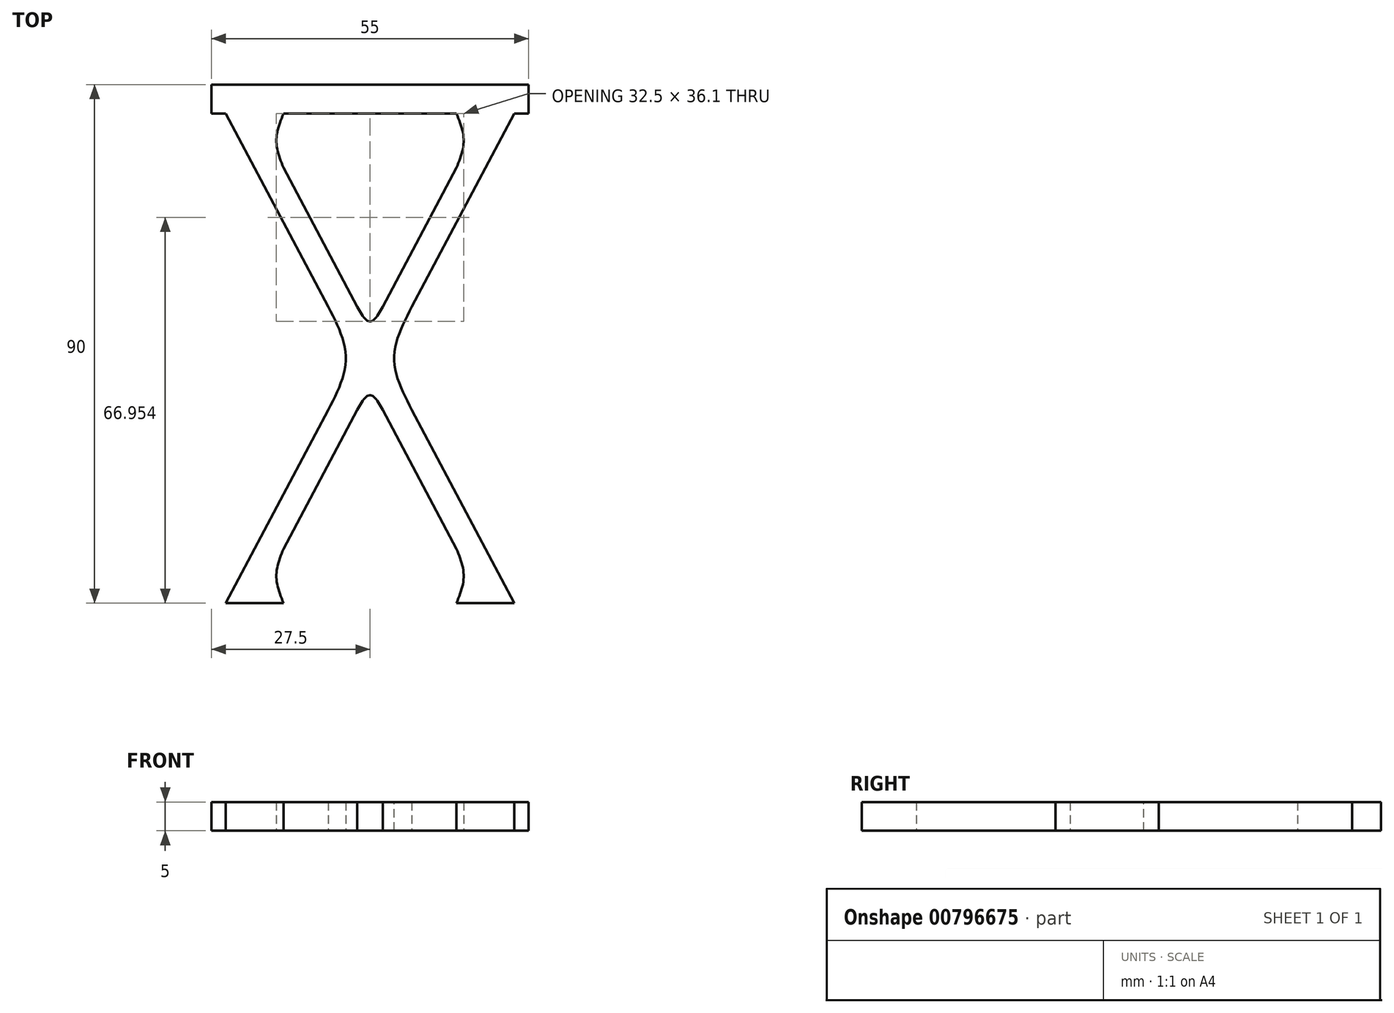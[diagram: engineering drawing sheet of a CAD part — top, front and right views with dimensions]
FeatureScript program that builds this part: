
annotation { "Feature Type Name" : "Feature", "Feature Type Description" : "" }
export const myFeature = defineFeature(function(context is Context, id is Id, definition is map)
    precondition{}
    {
        {
            var Q0;
            Q0=qCreatedBy(makeId("Top.planeOp"),FACE);
            var sketch = newSketch(context, id + "F0", { "sketchPlane" : qUnion([Q0])});
            skLineSegment(sketch, "E0.bottom", {"start": v(-698.92, -298.79) * mm, "end": v(-643.92, -298.79) * mm});
            skLineSegment(sketch, "E1", {"start": v(-696.42, -383.79) * mm, "end": v(-691.42, -383.79) * mm});
            skLineSegment(sketch, "E2", {"start": v(-691.42, -383.79) * mm, "end": v(-686.42, -383.79) * mm});
            skLineSegment(sketch, "E3", {"start": v(-646.42, -383.79) * mm, "end": v(-651.42, -383.79) * mm});
            skLineSegment(sketch, "E4", {"start": v(-651.42, -383.79) * mm, "end": v(-656.42, -383.79) * mm});
            skLineSegment(sketch, "E5", {"start": v(-698.92, -298.79) * mm, "end": v(-696.42, -298.79) * mm});
            skLineSegment(sketch, "E6", {"start": v(-696.42, -298.79) * mm, "end": v(-691.42, -298.79) * mm});
            skLineSegment(sketch, "E7", {"start": v(-691.42, -298.79) * mm, "end": v(-686.42, -298.79) * mm});
            skLineSegment(sketch, "E8", {"start": v(-643.92, -298.79) * mm, "end": v(-646.42, -298.79) * mm});
            skLineSegment(sketch, "E9", {"start": v(-646.42, -298.79) * mm, "end": v(-651.42, -298.79) * mm});
            skLineSegment(sketch, "E10", {"start": v(-651.42, -298.79) * mm, "end": v(-656.42, -298.79) * mm});
            skLineSegment(sketch, "E11", {"start": v(-646.42, -383.79) * mm, "end": v(-691.42, -298.79) * mm});
            skLineSegment(sketch, "E12", {"start": v(-646.42, -298.79) * mm, "end": v(-691.42, -383.79) * mm});
            skLineSegment(sketch, "E13", {"start": v(-696.42, -383.79) * mm, "end": v(-651.42, -298.79) * mm});
            skLineSegment(sketch, "E14", {"start": v(-696.42, -298.79) * mm, "end": v(-651.42, -383.79) * mm});
            skLineSegment(sketch, "E15", {"start": v(-686.42, -374.34) * mm, "end": v(-688.92, -379.06) * mm});
            skFitSpline(sketch, "E16", {"points": [v(-686.42, -383.79) * mm, v(-687.67, -379.06) * mm, v(-686.42, -374.34) * mm], "startDerivative": vector(-3.75, 9.44) * mm, "endDerivative": vector(3.75, 9.44) * mm});
            skFitSpline(sketch, "E17", {"points": [v(-656.42, -383.79) * mm, v(-655.17, -379.06) * mm, v(-656.42, -374.34) * mm], "startDerivative": vector(3.75, 9.44) * mm, "endDerivative": vector(-3.75, 9.44) * mm});
            skFitSpline(sketch, "E18", {"points": [v(-686.42, -298.79) * mm, v(-687.67, -303.5) * mm, v(-686.42, -308.23) * mm], "startDerivative": vector(-3.75, -9.44) * mm, "endDerivative": vector(3.75, -9.44) * mm});
            skFitSpline(sketch, "E19", {"points": [v(-656.42, -298.79) * mm, v(-655.17, -303.5) * mm, v(-656.42, -308.23) * mm], "startDerivative": vector(3.75, -9.44) * mm, "endDerivative": vector(-3.75, -9.44) * mm});
            skLineSegment(sketch, "E20", {"start": v(-673.92, -341.29) * mm, "end": v(-678.66, -332.34) * mm});
            skLineSegment(sketch, "E21", {"start": v(-678.66, -350.23) * mm, "end": v(-673.92, -341.29) * mm});
            skFitSpline(sketch, "E22", {"points": [v(-678.66, -332.34) * mm, v(-675.6, -341.29) * mm, v(-678.66, -350.23) * mm], "startDerivative": vector(9.19, -17.9) * mm, "endDerivative": vector(-9.19, -17.9) * mm});
            skFitSpline(sketch, "E23", {"points": [v(-664.18, -332.34) * mm, v(-667.24, -341.29) * mm, v(-664.18, -350.23) * mm], "startDerivative": vector(-9.18, -17.9) * mm, "endDerivative": vector(9.18, -17.9) * mm});
            skFitSpline(sketch, "E24", {"points": [v(-673.66, -332.34) * mm, v(-671.42, -334.89) * mm, v(-669.18, -332.34) * mm], "startDerivative": vector(4.47, -7.65) * mm, "endDerivative": vector(4.47, 7.65) * mm});
            skFitSpline(sketch, "E25", {"points": [v(-673.66, -350.23) * mm, v(-671.42, -347.68) * mm, v(-669.18, -350.23) * mm], "startDerivative": vector(4.47, 7.65) * mm, "endDerivative": vector(4.47, -7.65) * mm});
            skLineSegment(sketch, "E26.top", {"start": v(-698.92, -293.79) * mm, "end": v(-643.92, -293.79) * mm});
            skLineSegment(sketch, "E26.left", {"start": v(-698.92, -298.79) * mm, "end": v(-698.92, -293.79) * mm});
            skLineSegment(sketch, "E26.right", {"start": v(-643.92, -298.79) * mm, "end": v(-643.92, -293.79) * mm});
            skSolve(sketch);
        }
        {
            var Q0;
            Q0=qSketchRegion(id+"F0",true);
            var Q1;
            {var subQ0=sQuery(id+"F0.wireOp",EDGE,"E12");var subQ1=sQuery(id+"F0.wireOp",EDGE,"E11");var subQ2=makeQuery(id+"F0.imprint","INTERSECT",VERTEX,{"derivedFrom":[subQ1,subQ0]});Q1=makeQuery(id+"F0.imprint","IMPRINT",FACE,{"disambiguationData":[TD([[makeQuery(id+"F0.imprint","IMPRINT",EDGE,{"disambiguationData":[TD([[subQ2,-1.0]])],"derivedFrom":subQ1}),1.0]])]});}
            var Q2;
            {var subQ3=sQuery(id+"F0.wireOp",EDGE,"E18");Q2=makeQuery(id+"F0.imprint","IMPRINT",FACE,{"disambiguationData":[TD([[makeQuery(id+"F0.imprint","IMPRINT",EDGE,{"derivedFrom":subQ3}),-1.0]])]});}
            var Q3;
            {var subQ3=sQuery(id+"F0.wireOp",EDGE,"E19");Q3=makeQuery(id+"F0.imprint","IMPRINT",FACE,{"disambiguationData":[TD([[makeQuery(id+"F0.imprint","IMPRINT",EDGE,{"derivedFrom":subQ3}),1.0]])]});}
            var Q4;
            {var subQ0=sQuery(id+"F0.wireOp",EDGE,"E24");Q4=makeQuery(id+"F0.imprint","IMPRINT",FACE,{"disambiguationData":[TD([[makeQuery(id+"F0.imprint","IMPRINT",EDGE,{"derivedFrom":subQ0}),-1.0]])]});}
            extrude(context, id + "F1", {"entities" : qUnion([Q0, Q1, Q2, Q3, Q4]), "depth" : 5 * mm, "offsetDistance" : 25.4 * mm});
        }
    });
